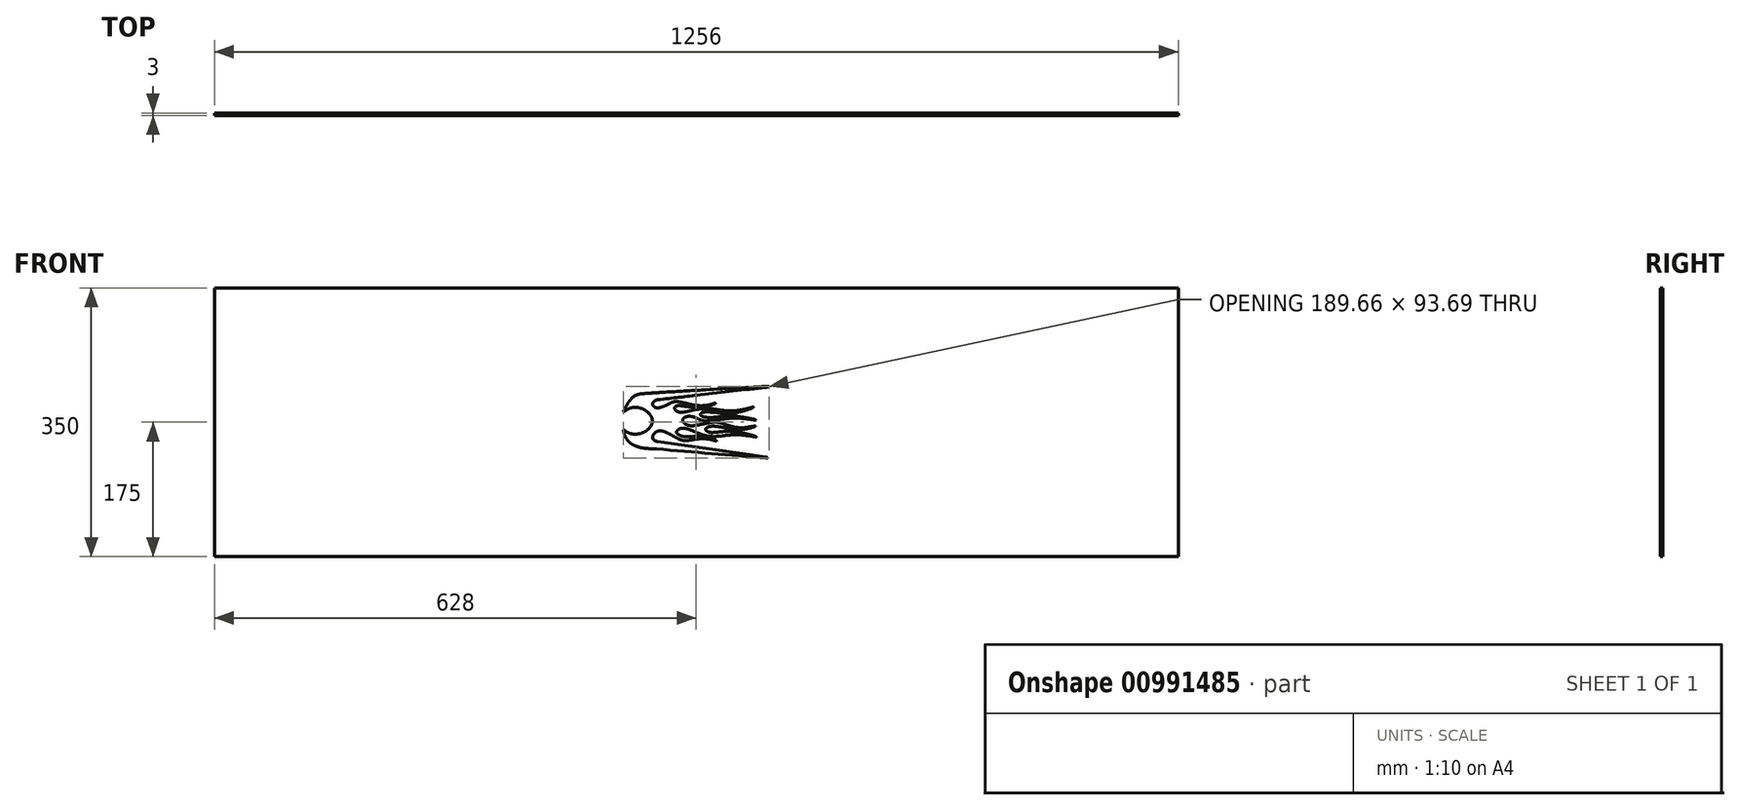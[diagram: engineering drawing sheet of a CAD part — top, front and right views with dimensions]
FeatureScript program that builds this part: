
annotation { "Feature Type Name" : "Feature", "Feature Type Description" : "" }
export const myFeature = defineFeature(function(context is Context, id is Id, definition is map)
    precondition{}
    {
        {
            var Q0;
            Q0=qCreatedBy(makeId("Front.planeOp"),FACE);
            var sketch = newSketch(context, id + "F0", { "sketchPlane" : qUnion([Q0])});
            skLineSegment(sketch, "E0.bottom", {"start": v(628, -175) * mm, "end": v(-628, -175) * mm});
            skLineSegment(sketch, "E0.top", {"start": v(628, 175) * mm, "end": v(-628, 175) * mm});
            skLineSegment(sketch, "E0.left", {"start": v(628, -175) * mm, "end": v(628, 175) * mm});
            skLineSegment(sketch, "E0.right", {"start": v(-628, -175) * mm, "end": v(-628, 175) * mm});
            skPoint(sketch, "E0.middle", {"position": v(0, 0) * mm});
            skArc(sketch, "E1", {"start": v(-49.97, 29.36) * mm, "mid": v(-22.29, 32.51) * mm, "end": v(5.39, 35.72) * mm});
            skArc(sketch, "E2", {"start": v(5.39, 35.72) * mm, "mid": v(48.23, 40.7) * mm, "end": v(91.08, 45.54) * mm});
            skArc(sketch, "E3", {"start": v(91.08, 45.54) * mm, "mid": v(92.6, 45.75) * mm, "end": v(94.1, 46.07) * mm});
            skArc(sketch, "E4", {"start": v(94.1, 46.07) * mm, "mid": v(94.42, 46.17) * mm, "end": v(94.72, 46.32) * mm});
            skArc(sketch, "E5", {"start": v(94.72, 46.32) * mm, "mid": v(94.82, 46.41) * mm, "end": v(94.81, 46.54) * mm});
            skArc(sketch, "E6", {"start": v(94.81, 46.54) * mm, "mid": v(94.26, 46.77) * mm, "end": v(93.66, 46.82) * mm});
            skArc(sketch, "E7", {"start": v(93.66, 46.82) * mm, "mid": v(92.36, 46.84) * mm, "end": v(91.07, 46.76) * mm});
            skArc(sketch, "E8", {"start": v(91.07, 46.76) * mm, "mid": v(90.64, 46.73) * mm, "end": v(90.2, 46.7) * mm});
            skArc(sketch, "E9", {"start": v(90.2, 46.7) * mm, "mid": v(48.75, 44.38) * mm, "end": v(7.3, 42.02) * mm});
            skArc(sketch, "E10", {"start": v(7.3, 42.02) * mm, "mid": v(-18.63, 40.5) * mm, "end": v(-44.56, 38.95) * mm});
            skArc(sketch, "E11", {"start": v(-44.56, 38.95) * mm, "mid": v(-53.35, 38.4) * mm, "end": v(-62.13, 37.81) * mm});
            skArc(sketch, "E12", {"start": v(-62.13, 37.81) * mm, "mid": v(-66.04, 37.54) * mm, "end": v(-69.95, 37.17) * mm});
            skArc(sketch, "E13", {"start": v(-69.95, 37.17) * mm, "mid": v(-78.19, 35.35) * mm, "end": v(-85.02, 30.4) * mm});
            skArc(sketch, "E14", {"start": v(-85.02, 30.4) * mm, "mid": v(-87.57, 27.3) * mm, "end": v(-89.78, 23.94) * mm});
            skArc(sketch, "E15", {"start": v(-89.78, 23.94) * mm, "mid": v(-91.8, 20.36) * mm, "end": v(-93.7, 16.7) * mm});
            skArc(sketch, "E16", {"start": v(-93.7, 16.7) * mm, "mid": v(-93.9, 16.3) * mm, "end": v(-94.1, 15.91) * mm});
            skArc(sketch, "E17", {"start": v(-94.1, 15.91) * mm, "mid": v(-94.48, 15.13) * mm, "end": v(-94.71, 14.3) * mm});
            skArc(sketch, "E18", {"start": v(-94.71, 14.3) * mm, "mid": v(-94.68, 14) * mm, "end": v(-94.42, 13.85) * mm});
            skArc(sketch, "E19", {"start": v(-94.42, 13.85) * mm, "mid": v(-93.65, 14.08) * mm, "end": v(-92.96, 14.48) * mm});
            skArc(sketch, "E20", {"start": v(-92.96, 14.48) * mm, "mid": v(-92.85, 14.55) * mm, "end": v(-92.73, 14.61) * mm});
            skArc(sketch, "E21", {"start": v(-92.73, 14.61) * mm, "mid": v(-87.36, 17.9) * mm, "end": v(-81.24, 19.36) * mm});
            skArc(sketch, "E22", {"start": v(-81.24, 19.36) * mm, "mid": v(-75.37, 19.02) * mm, "end": v(-69.75, 17.24) * mm});
            skArc(sketch, "E23", {"start": v(-69.75, 17.24) * mm, "mid": v(-64.93, 14.44) * mm, "end": v(-60.85, 10.63) * mm});
            skArc(sketch, "E24", {"start": v(-60.85, 10.63) * mm, "mid": v(-59.37, 8.6) * mm, "end": v(-58.18, 6.38) * mm});
            skArc(sketch, "E25", {"start": v(-58.18, 6.38) * mm, "mid": v(-57.44, 4.2) * mm, "end": v(-57.13, 1.9) * mm});
            skArc(sketch, "E26", {"start": v(-57.13, 1.9) * mm, "mid": v(-57.38, -0.44) * mm, "end": v(-58.06, -2.7) * mm});
            skArc(sketch, "E27", {"start": v(-58.06, -2.7) * mm, "mid": v(-59.2, -4.92) * mm, "end": v(-60.65, -6.95) * mm});
            skArc(sketch, "E28", {"start": v(-60.65, -6.95) * mm, "mid": v(-64.68, -10.72) * mm, "end": v(-69.48, -13.45) * mm});
            skArc(sketch, "E29", {"start": v(-69.48, -13.45) * mm, "mid": v(-75.15, -15.17) * mm, "end": v(-81.07, -15.5) * mm});
            skArc(sketch, "E30", {"start": v(-81.07, -15.5) * mm, "mid": v(-87.28, -14.14) * mm, "end": v(-92.84, -11.04) * mm});
            skArc(sketch, "E31", {"start": v(-92.84, -11.04) * mm, "mid": v(-93.32, -10.6) * mm, "end": v(-93.83, -10.2) * mm});
            skArc(sketch, "E32", {"start": v(-93.83, -10.2) * mm, "mid": v(-94.15, -10) * mm, "end": v(-94.53, -9.95) * mm});
            skArc(sketch, "E33", {"start": v(-94.53, -9.95) * mm, "mid": v(-94.78, -10.21) * mm, "end": v(-94.82, -10.58) * mm});
            skArc(sketch, "E34", {"start": v(-94.82, -10.58) * mm, "mid": v(-94.77, -11.47) * mm, "end": v(-94.6, -12.36) * mm});
            skArc(sketch, "E35", {"start": v(-94.6, -12.36) * mm, "mid": v(-93.25, -17.04) * mm, "end": v(-91.06, -21.4) * mm});
            skArc(sketch, "E36", {"start": v(-91.06, -21.4) * mm, "mid": v(-88.7, -24.49) * mm, "end": v(-85.85, -27.13) * mm});
            skArc(sketch, "E37", {"start": v(-85.85, -27.13) * mm, "mid": v(-83.19, -28.92) * mm, "end": v(-80.33, -30.38) * mm});
            skArc(sketch, "E38", {"start": v(-80.33, -30.38) * mm, "mid": v(-78.13, -31.26) * mm, "end": v(-75.88, -32.02) * mm});
            skArc(sketch, "E39", {"start": v(-75.88, -32.02) * mm, "mid": v(-75.4, -32.17) * mm, "end": v(-74.93, -32.33) * mm});
            skArc(sketch, "E40", {"start": v(-74.93, -32.33) * mm, "mid": v(-72.38, -33.1) * mm, "end": v(-69.75, -33.57) * mm});
            skArc(sketch, "E41", {"start": v(-69.75, -33.57) * mm, "mid": v(-66.23, -34) * mm, "end": v(-62.7, -34.32) * mm});
            skArc(sketch, "E42", {"start": v(-62.7, -34.32) * mm, "mid": v(-57.3, -34.63) * mm, "end": v(-51.9, -34.72) * mm});
            skArc(sketch, "E43", {"start": v(-51.9, -34.72) * mm, "mid": v(19.58, -40.8) * mm, "end": v(91.07, -46.8) * mm});
            skArc(sketch, "E44", {"start": v(91.07, -46.8) * mm, "mid": v(91.84, -46.84) * mm, "end": v(92.6, -46.75) * mm});
            skArc(sketch, "E45", {"start": v(92.6, -46.75) * mm, "mid": v(92.87, -46.66) * mm, "end": v(92.98, -46.4) * mm});
            skArc(sketch, "E46", {"start": v(92.98, -46.4) * mm, "mid": v(92.75, -46.12) * mm, "end": v(92.44, -45.94) * mm});
            skArc(sketch, "E47", {"start": v(92.44, -45.94) * mm, "mid": v(91.83, -45.73) * mm, "end": v(91.2, -45.6) * mm});
            skArc(sketch, "E48", {"start": v(91.2, -45.6) * mm, "mid": v(56.21, -40.64) * mm, "end": v(21.24, -35.54) * mm});
            skArc(sketch, "E49", {"start": v(21.24, -35.54) * mm, "mid": v(-14.89, -30.26) * mm, "end": v(-51.01, -24.96) * mm});
            skArc(sketch, "E50", {"start": v(-51.01, -24.96) * mm, "mid": v(-52.44, -24.6) * mm, "end": v(-53.8, -24.06) * mm});
            skArc(sketch, "E51", {"start": v(-53.8, -24.06) * mm, "mid": v(-54.77, -23.47) * mm, "end": v(-55.6, -22.71) * mm});
            skArc(sketch, "E52", {"start": v(-55.6, -22.71) * mm, "mid": v(-56.54, -21.08) * mm, "end": v(-56.76, -19.21) * mm});
            skArc(sketch, "E53", {"start": v(-56.76, -19.21) * mm, "mid": v(-55.5, -15.57) * mm, "end": v(-52.8, -12.83) * mm});
            skArc(sketch, "E54", {"start": v(-52.8, -12.83) * mm, "mid": v(-48.6, -11.31) * mm, "end": v(-44.12, -11.5) * mm});
            skArc(sketch, "E55", {"start": v(-44.12, -11.5) * mm, "mid": v(-42.1, -12.07) * mm, "end": v(-40.12, -12.82) * mm});
            skArc(sketch, "E56", {"start": v(-40.12, -12.82) * mm, "mid": v(-38.31, -13.65) * mm, "end": v(-36.53, -14.54) * mm});
            skArc(sketch, "E57", {"start": v(-36.53, -14.54) * mm, "mid": v(-35, -15.31) * mm, "end": v(-33.43, -16) * mm});
            skArc(sketch, "E58", {"start": v(-33.43, -16) * mm, "mid": v(-28.86, -18.7) * mm, "end": v(-24.18, -21.22) * mm});
            skArc(sketch, "E59", {"start": v(-24.18, -21.22) * mm, "mid": v(-21.02, -22.62) * mm, "end": v(-17.7, -23.6) * mm});
            skArc(sketch, "E60", {"start": v(-17.7, -23.6) * mm, "mid": v(-14.67, -23.93) * mm, "end": v(-11.63, -23.82) * mm});
            skArc(sketch, "E61", {"start": v(-11.63, -23.82) * mm, "mid": v(-7.64, -23.29) * mm, "end": v(-3.66, -22.6) * mm});
            skArc(sketch, "E62", {"start": v(-3.66, -22.6) * mm, "mid": v(-3.63, -22.6) * mm, "end": v(-3.6, -22.6) * mm});
            skArc(sketch, "E63", {"start": v(-3.6, -22.6) * mm, "mid": v(4.1, -21.59) * mm, "end": v(11.85, -21.58) * mm});
            skArc(sketch, "E64", {"start": v(11.85, -21.58) * mm, "mid": v(15.03, -21.86) * mm, "end": v(18.18, -22.35) * mm});
            skArc(sketch, "E65", {"start": v(18.18, -22.35) * mm, "mid": v(20.5, -22.87) * mm, "end": v(22.78, -23.6) * mm});
            skArc(sketch, "E66", {"start": v(22.78, -23.6) * mm, "mid": v(24.05, -24.01) * mm, "end": v(25.34, -24.3) * mm});
            skArc(sketch, "E67", {"start": v(25.34, -24.3) * mm, "mid": v(25.7, -24.33) * mm, "end": v(26.05, -24.32) * mm});
            skArc(sketch, "E68", {"start": v(26.05, -24.32) * mm, "mid": v(26.23, -24.29) * mm, "end": v(26.36, -24.18) * mm});
            skArc(sketch, "E69", {"start": v(26.36, -24.18) * mm, "mid": v(26.35, -24.02) * mm, "end": v(26.25, -23.9) * mm});
            skArc(sketch, "E70", {"start": v(26.25, -23.9) * mm, "mid": v(26, -23.68) * mm, "end": v(25.7, -23.5) * mm});
            skArc(sketch, "E71", {"start": v(25.7, -23.5) * mm, "mid": v(24.5, -22.95) * mm, "end": v(23.25, -22.53) * mm});
            skArc(sketch, "E72", {"start": v(23.25, -22.53) * mm, "mid": v(18.62, -21) * mm, "end": v(13.86, -19.88) * mm});
            skArc(sketch, "E73", {"start": v(13.86, -19.88) * mm, "mid": v(6.65, -18.77) * mm, "end": v(-0.64, -18.4) * mm});
            skArc(sketch, "E74", {"start": v(-0.64, -18.4) * mm, "mid": v(-2.99, -18.5) * mm, "end": v(-5.33, -18.62) * mm});
            skArc(sketch, "E75", {"start": v(-5.33, -18.62) * mm, "mid": v(-10.14, -18.85) * mm, "end": v(-14.96, -18.7) * mm});
            skArc(sketch, "E76", {"start": v(-14.96, -18.7) * mm, "mid": v(-19.53, -17.83) * mm, "end": v(-23.77, -15.9) * mm});
            skArc(sketch, "E77", {"start": v(-23.77, -15.9) * mm, "mid": v(-24.71, -15.01) * mm, "end": v(-25.37, -13.9) * mm});
            skArc(sketch, "E78", {"start": v(-25.37, -13.9) * mm, "mid": v(-25.55, -12.9) * mm, "end": v(-25.37, -11.9) * mm});
            skArc(sketch, "E79", {"start": v(-25.37, -11.9) * mm, "mid": v(-24.82, -10.88) * mm, "end": v(-24.04, -10.04) * mm});
            skArc(sketch, "E80", {"start": v(-24.04, -10.04) * mm, "mid": v(-22.88, -9.19) * mm, "end": v(-21.62, -8.51) * mm});
            skArc(sketch, "E81", {"start": v(-21.62, -8.51) * mm, "mid": v(-19.78, -7.95) * mm, "end": v(-17.87, -7.73) * mm});
            skArc(sketch, "E82", {"start": v(-17.87, -7.73) * mm, "mid": v(-15.9, -7.8) * mm, "end": v(-13.94, -8.1) * mm});
            skArc(sketch, "E83", {"start": v(-13.94, -8.1) * mm, "mid": v(-9.95, -9.23) * mm, "end": v(-6.06, -10.68) * mm});
            skArc(sketch, "E84", {"start": v(-6.06, -10.68) * mm, "mid": v(-4.72, -11.2) * mm, "end": v(-3.38, -11.7) * mm});
            skArc(sketch, "E85", {"start": v(-3.38, -11.7) * mm, "mid": v(-3.08, -11.82) * mm, "end": v(-2.79, -11.95) * mm});
            skArc(sketch, "E86", {"start": v(-2.79, -11.95) * mm, "mid": v(2.14, -14.05) * mm, "end": v(7.15, -15.93) * mm});
            skArc(sketch, "E87", {"start": v(7.15, -15.93) * mm, "mid": v(12.53, -17.47) * mm, "end": v(18.06, -18.31) * mm});
            skArc(sketch, "E88", {"start": v(18.06, -18.31) * mm, "mid": v(22.97, -18.5) * mm, "end": v(27.89, -18.35) * mm});
            skArc(sketch, "E89", {"start": v(27.89, -18.35) * mm, "mid": v(32.17, -17.96) * mm, "end": v(36.43, -17.45) * mm});
            skArc(sketch, "E90", {"start": v(36.43, -17.45) * mm, "mid": v(44.4, -16.58) * mm, "end": v(52.42, -16.3) * mm});
            skArc(sketch, "E91", {"start": v(52.42, -16.3) * mm, "mid": v(57.84, -16.5) * mm, "end": v(63.24, -16.99) * mm});
            skArc(sketch, "E92", {"start": v(63.24, -16.99) * mm, "mid": v(70.26, -17.96) * mm, "end": v(77.23, -19.23) * mm});
            skArc(sketch, "E93", {"start": v(77.23, -19.23) * mm, "mid": v(77.64, -19.3) * mm, "end": v(78.07, -19.33) * mm});
            skArc(sketch, "E94", {"start": v(78.07, -19.33) * mm, "mid": v(78.26, -19.3) * mm, "end": v(78.42, -19.19) * mm});
            skArc(sketch, "E95", {"start": v(78.42, -19.19) * mm, "mid": v(78.37, -19) * mm, "end": v(78.24, -18.88) * mm});
            skArc(sketch, "E96", {"start": v(78.24, -18.88) * mm, "mid": v(77.88, -18.65) * mm, "end": v(77.5, -18.47) * mm});
            skArc(sketch, "E97", {"start": v(77.5, -18.47) * mm, "mid": v(75.04, -17.64) * mm, "end": v(72.54, -16.93) * mm});
            skArc(sketch, "E98", {"start": v(72.54, -16.93) * mm, "mid": v(68.67, -15.94) * mm, "end": v(64.79, -15.02) * mm});
            skArc(sketch, "E99", {"start": v(64.79, -15.02) * mm, "mid": v(56.1, -13.24) * mm, "end": v(47.34, -11.91) * mm});
            skArc(sketch, "E100", {"start": v(47.34, -11.91) * mm, "mid": v(42.94, -11.7) * mm, "end": v(38.54, -11.84) * mm});
            skArc(sketch, "E101", {"start": v(38.54, -11.84) * mm, "mid": v(33.87, -12.22) * mm, "end": v(29.22, -12.7) * mm});
            skArc(sketch, "E102", {"start": v(29.22, -12.7) * mm, "mid": v(25.97, -13.05) * mm, "end": v(22.71, -13.33) * mm});
            skArc(sketch, "E103", {"start": v(22.71, -13.33) * mm, "mid": v(20.48, -13.43) * mm, "end": v(18.25, -13.28) * mm});
            skArc(sketch, "E104", {"start": v(18.25, -13.28) * mm, "mid": v(16.63, -12.85) * mm, "end": v(15.05, -12.28) * mm});
            skArc(sketch, "E105", {"start": v(15.05, -12.28) * mm, "mid": v(14.02, -11.8) * mm, "end": v(13.07, -11.17) * mm});
            skArc(sketch, "E106", {"start": v(13.07, -11.17) * mm, "mid": v(12.54, -10.64) * mm, "end": v(12.17, -9.99) * mm});
            skArc(sketch, "E107", {"start": v(12.17, -9.99) * mm, "mid": v(12.07, -9.4) * mm, "end": v(12.18, -8.82) * mm});
            skArc(sketch, "E108", {"start": v(12.18, -8.82) * mm, "mid": v(13.08, -7.58) * mm, "end": v(14.35, -6.71) * mm});
            skArc(sketch, "E109", {"start": v(14.35, -6.71) * mm, "mid": v(16.3, -5.87) * mm, "end": v(18.35, -5.34) * mm});
            skArc(sketch, "E110", {"start": v(18.35, -5.34) * mm, "mid": v(20.83, -5.1) * mm, "end": v(23.32, -5.1) * mm});
            skArc(sketch, "E111", {"start": v(23.32, -5.1) * mm, "mid": v(26.2, -5.31) * mm, "end": v(29.05, -5.67) * mm});
            skArc(sketch, "E112", {"start": v(29.05, -5.67) * mm, "mid": v(35.07, -6.7) * mm, "end": v(41.04, -7.93) * mm});
            skArc(sketch, "E113", {"start": v(41.04, -7.93) * mm, "mid": v(46.1, -8.99) * mm, "end": v(51.19, -9.77) * mm});
            skArc(sketch, "E114", {"start": v(51.19, -9.77) * mm, "mid": v(57.58, -9.66) * mm, "end": v(63.92, -8.85) * mm});
            skArc(sketch, "E115", {"start": v(63.92, -8.85) * mm, "mid": v(70.13, -7.48) * mm, "end": v(76.2, -5.61) * mm});
            skArc(sketch, "E116", {"start": v(76.2, -5.61) * mm, "mid": v(76.57, -5.47) * mm, "end": v(76.9, -5.28) * mm});
            skArc(sketch, "E117", {"start": v(76.9, -5.28) * mm, "mid": v(77.04, -5.17) * mm, "end": v(77.1, -5) * mm});
            skArc(sketch, "E118", {"start": v(77.1, -5) * mm, "mid": v(76.99, -4.89) * mm, "end": v(76.83, -4.86) * mm});
            skArc(sketch, "E119", {"start": v(76.83, -4.86) * mm, "mid": v(76.46, -4.86) * mm, "end": v(76.1, -4.91) * mm});
            skArc(sketch, "E120", {"start": v(76.1, -4.91) * mm, "mid": v(76.04, -4.92) * mm, "end": v(75.98, -4.93) * mm});
            skArc(sketch, "E121", {"start": v(75.98, -4.93) * mm, "mid": v(71.08, -5.82) * mm, "end": v(66.15, -6.59) * mm});
            skArc(sketch, "E122", {"start": v(66.15, -6.59) * mm, "mid": v(58.72, -7.25) * mm, "end": v(51.3, -6.57) * mm});
            skArc(sketch, "E123", {"start": v(51.3, -6.57) * mm, "mid": v(44.85, -5.06) * mm, "end": v(38.52, -3.08) * mm});
            skArc(sketch, "E124", {"start": v(38.52, -3.08) * mm, "mid": v(34.64, -1.84) * mm, "end": v(30.72, -0.74) * mm});
            skArc(sketch, "E125", {"start": v(30.72, -0.74) * mm, "mid": v(27.03, -0.03) * mm, "end": v(23.27, 0.22) * mm});
            skArc(sketch, "E126", {"start": v(23.27, 0.22) * mm, "mid": v(20.42, -0.06) * mm, "end": v(17.6, -0.53) * mm});
            skArc(sketch, "E127", {"start": v(17.6, -0.53) * mm, "mid": v(13.73, -1.28) * mm, "end": v(9.87, -2.07) * mm});
            skArc(sketch, "E128", {"start": v(9.87, -2.07) * mm, "mid": v(5.06, -3.06) * mm, "end": v(0.23, -3.96) * mm});
            skArc(sketch, "E129", {"start": v(0.23, -3.96) * mm, "mid": v(-1.8, -4.28) * mm, "end": v(-3.83, -4.54) * mm});
            skArc(sketch, "E130", {"start": v(-3.83, -4.54) * mm, "mid": v(-5.35, -4.67) * mm, "end": v(-6.88, -4.67) * mm});
            skArc(sketch, "E131", {"start": v(-6.88, -4.67) * mm, "mid": v(-10.85, -3.87) * mm, "end": v(-14.52, -2.16) * mm});
            skArc(sketch, "E132", {"start": v(-14.52, -2.16) * mm, "mid": v(-15.65, -1.27) * mm, "end": v(-16.62, -0.2) * mm});
            skArc(sketch, "E133", {"start": v(-16.62, -0.2) * mm, "mid": v(-17.22, 0.82) * mm, "end": v(-17.56, 1.94) * mm});
            skArc(sketch, "E134", {"start": v(-17.56, 1.94) * mm, "mid": v(-17.3, 4.12) * mm, "end": v(-15.91, 5.83) * mm});
            skArc(sketch, "E135", {"start": v(-15.91, 5.83) * mm, "mid": v(-14.66, 6.6) * mm, "end": v(-13.29, 7.12) * mm});
            skArc(sketch, "E136", {"start": v(-13.29, 7.12) * mm, "mid": v(-11.38, 7.53) * mm, "end": v(-9.44, 7.68) * mm});
            skArc(sketch, "E137", {"start": v(-9.44, 7.68) * mm, "mid": v(-6.11, 7.46) * mm, "end": v(-2.85, 6.72) * mm});
            skArc(sketch, "E138", {"start": v(-2.85, 6.72) * mm, "mid": v(-0.4, 5.77) * mm, "end": v(1.95, 4.6) * mm});
            skArc(sketch, "E139", {"start": v(1.95, 4.6) * mm, "mid": v(5.08, 3.1) * mm, "end": v(8.39, 2.02) * mm});
            skArc(sketch, "E140", {"start": v(8.39, 2.02) * mm, "mid": v(10.6, 1.61) * mm, "end": v(12.83, 1.43) * mm});
            skArc(sketch, "E141", {"start": v(12.83, 1.43) * mm, "mid": v(15.8, 1.45) * mm, "end": v(18.74, 1.7) * mm});
            skArc(sketch, "E142", {"start": v(18.74, 1.7) * mm, "mid": v(21.42, 2.12) * mm, "end": v(24.1, 2.56) * mm});
            skArc(sketch, "E143", {"start": v(24.1, 2.56) * mm, "mid": v(32.98, 3.95) * mm, "end": v(41.9, 5.02) * mm});
            skArc(sketch, "E144", {"start": v(41.9, 5.02) * mm, "mid": v(51.02, 5.47) * mm, "end": v(60.14, 4.97) * mm});
            skArc(sketch, "E145", {"start": v(60.14, 4.97) * mm, "mid": v(68.02, 4.05) * mm, "end": v(75.88, 2.92) * mm});
            skArc(sketch, "E146", {"start": v(75.88, 2.92) * mm, "mid": v(76.5, 2.83) * mm, "end": v(77.14, 2.8) * mm});
            skArc(sketch, "E147", {"start": v(77.14, 2.8) * mm, "mid": v(77.35, 2.82) * mm, "end": v(77.5, 2.98) * mm});
            skArc(sketch, "E148", {"start": v(77.5, 2.98) * mm, "mid": v(77.35, 3.17) * mm, "end": v(77.13, 3.29) * mm});
            skArc(sketch, "E149", {"start": v(77.13, 3.29) * mm, "mid": v(76.65, 3.47) * mm, "end": v(76.16, 3.58) * mm});
            skArc(sketch, "E150", {"start": v(76.16, 3.58) * mm, "mid": v(75.47, 3.72) * mm, "end": v(74.79, 3.86) * mm});
            skArc(sketch, "E151", {"start": v(74.79, 3.86) * mm, "mid": v(67.42, 5.33) * mm, "end": v(60.02, 6.65) * mm});
            skArc(sketch, "E152", {"start": v(60.02, 6.65) * mm, "mid": v(55.46, 7.36) * mm, "end": v(50.89, 7.95) * mm});
            skArc(sketch, "E153", {"start": v(50.89, 7.95) * mm, "mid": v(47.14, 8.3) * mm, "end": v(43.37, 8.38) * mm});
            skArc(sketch, "E154", {"start": v(43.37, 8.38) * mm, "mid": v(40.5, 8.3) * mm, "end": v(37.62, 8.07) * mm});
            skArc(sketch, "E155", {"start": v(37.62, 8.07) * mm, "mid": v(34.46, 7.71) * mm, "end": v(31.3, 7.31) * mm});
            skArc(sketch, "E156", {"start": v(31.3, 7.31) * mm, "mid": v(26.2, 6.68) * mm, "end": v(21.07, 6.23) * mm});
            skArc(sketch, "E157", {"start": v(21.07, 6.23) * mm, "mid": v(16.22, 6.14) * mm, "end": v(11.4, 6.64) * mm});
            skArc(sketch, "E158", {"start": v(11.4, 6.64) * mm, "mid": v(9, 7.24) * mm, "end": v(6.76, 8.29) * mm});
            skArc(sketch, "E159", {"start": v(6.76, 8.29) * mm, "mid": v(6.16, 8.75) * mm, "end": v(5.66, 9.33) * mm});
            skArc(sketch, "E160", {"start": v(5.66, 9.33) * mm, "mid": v(5.41, 9.85) * mm, "end": v(5.35, 10.42) * mm});
            skArc(sketch, "E161", {"start": v(5.35, 10.42) * mm, "mid": v(5.5, 10.97) * mm, "end": v(5.82, 11.45) * mm});
            skArc(sketch, "E162", {"start": v(5.82, 11.45) * mm, "mid": v(6.4, 11.96) * mm, "end": v(7.05, 12.35) * mm});
            skArc(sketch, "E163", {"start": v(7.05, 12.35) * mm, "mid": v(9.35, 13.11) * mm, "end": v(11.75, 13.41) * mm});
            skArc(sketch, "E164", {"start": v(11.75, 13.41) * mm, "mid": v(15.6, 13.4) * mm, "end": v(19.44, 13.2) * mm});
            skArc(sketch, "E165", {"start": v(19.44, 13.2) * mm, "mid": v(23.59, 12.92) * mm, "end": v(27.72, 12.47) * mm});
            skArc(sketch, "E166", {"start": v(27.72, 12.47) * mm, "mid": v(39.73, 11.7) * mm, "end": v(51.73, 12.63) * mm});
            skArc(sketch, "E167", {"start": v(51.73, 12.63) * mm, "mid": v(62.5, 15.04) * mm, "end": v(72.9, 18.74) * mm});
            skArc(sketch, "E168", {"start": v(72.9, 18.74) * mm, "mid": v(73.48, 18.94) * mm, "end": v(74.05, 19.2) * mm});
            skArc(sketch, "E169", {"start": v(74.05, 19.2) * mm, "mid": v(74.3, 19.35) * mm, "end": v(74.46, 19.58) * mm});
            skArc(sketch, "E170", {"start": v(74.46, 19.58) * mm, "mid": v(74.31, 19.74) * mm, "end": v(74.1, 19.75) * mm});
            skArc(sketch, "E171", {"start": v(74.1, 19.75) * mm, "mid": v(73.49, 19.7) * mm, "end": v(72.9, 19.57) * mm});
            skArc(sketch, "E172", {"start": v(72.9, 19.57) * mm, "mid": v(63.37, 17.07) * mm, "end": v(53.68, 15.27) * mm});
            skArc(sketch, "E173", {"start": v(53.68, 15.27) * mm, "mid": v(44.03, 14.6) * mm, "end": v(34.4, 15.4) * mm});
            skArc(sketch, "E174", {"start": v(34.4, 15.4) * mm, "mid": v(33.15, 15.59) * mm, "end": v(31.9, 15.77) * mm});
            skArc(sketch, "E175", {"start": v(31.9, 15.77) * mm, "mid": v(26.34, 16.6) * mm, "end": v(20.77, 17.31) * mm});
            skArc(sketch, "E176", {"start": v(20.77, 17.31) * mm, "mid": v(16.06, 17.7) * mm, "end": v(11.33, 17.8) * mm});
            skArc(sketch, "E177", {"start": v(11.33, 17.8) * mm, "mid": v(6.17, 17.48) * mm, "end": v(1.05, 16.8) * mm});
            skArc(sketch, "E178", {"start": v(1.05, 16.8) * mm, "mid": v(-5.82, 15.47) * mm, "end": v(-12.64, 13.89) * mm});
            skArc(sketch, "E179", {"start": v(-12.64, 13.89) * mm, "mid": v(-12.98, 13.82) * mm, "end": v(-13.33, 13.75) * mm});
            skArc(sketch, "E180", {"start": v(-13.33, 13.75) * mm, "mid": v(-16.32, 13.2) * mm, "end": v(-19.35, 12.93) * mm});
            skArc(sketch, "E181", {"start": v(-19.35, 12.93) * mm, "mid": v(-22.45, 13.21) * mm, "end": v(-25.37, 14.27) * mm});
            skArc(sketch, "E182", {"start": v(-25.37, 14.27) * mm, "mid": v(-27.32, 15.87) * mm, "end": v(-28.22, 18.24) * mm});
            skArc(sketch, "E183", {"start": v(-28.22, 18.24) * mm, "mid": v(-27.94, 19.5) * mm, "end": v(-27.1, 20.5) * mm});
            skArc(sketch, "E184", {"start": v(-27.1, 20.5) * mm, "mid": v(-26.33, 20.98) * mm, "end": v(-25.49, 21.32) * mm});
            skArc(sketch, "E185", {"start": v(-25.49, 21.32) * mm, "mid": v(-24.26, 21.62) * mm, "end": v(-23, 21.78) * mm});
            skArc(sketch, "E186", {"start": v(-23, 21.78) * mm, "mid": v(-21.84, 21.75) * mm, "end": v(-20.7, 21.62) * mm});
            skArc(sketch, "E187", {"start": v(-20.7, 21.62) * mm, "mid": v(-18.75, 21.37) * mm, "end": v(-16.8, 21.09) * mm});
            skArc(sketch, "E188", {"start": v(-16.8, 21.09) * mm, "mid": v(-9.62, 20.12) * mm, "end": v(-2.4, 19.46) * mm});
            skArc(sketch, "E189", {"start": v(-2.4, 19.46) * mm, "mid": v(1.54, 19.32) * mm, "end": v(5.48, 19.4) * mm});
            skArc(sketch, "E190", {"start": v(5.48, 19.4) * mm, "mid": v(9.07, 19.73) * mm, "end": v(12.6, 20.44) * mm});
            skArc(sketch, "E191", {"start": v(12.6, 20.44) * mm, "mid": v(15.62, 21.14) * mm, "end": v(18.6, 21.93) * mm});
            skArc(sketch, "E192", {"start": v(18.6, 21.93) * mm, "mid": v(21.41, 22.85) * mm, "end": v(24.14, 24) * mm});
            skArc(sketch, "E193", {"start": v(24.14, 24) * mm, "mid": v(24.52, 24.2) * mm, "end": v(24.86, 24.47) * mm});
            skArc(sketch, "E194", {"start": v(24.86, 24.47) * mm, "mid": v(25, 24.62) * mm, "end": v(25.04, 24.83) * mm});
            skArc(sketch, "E195", {"start": v(25.04, 24.83) * mm, "mid": v(24.9, 24.96) * mm, "end": v(24.7, 24.98) * mm});
            skArc(sketch, "E196", {"start": v(24.7, 24.98) * mm, "mid": v(24.27, 24.92) * mm, "end": v(23.85, 24.8) * mm});
            skArc(sketch, "E197", {"start": v(23.85, 24.8) * mm, "mid": v(20.09, 23.58) * mm, "end": v(16.26, 22.59) * mm});
            skArc(sketch, "E198", {"start": v(16.26, 22.59) * mm, "mid": v(12.22, 21.88) * mm, "end": v(8.14, 21.54) * mm});
            skArc(sketch, "E199", {"start": v(8.14, 21.54) * mm, "mid": v(3.4, 21.6) * mm, "end": v(-1.32, 22.09) * mm});
            skArc(sketch, "E200", {"start": v(-1.32, 22.09) * mm, "mid": v(-7.15, 23.19) * mm, "end": v(-12.9, 24.7) * mm});
            skArc(sketch, "E201", {"start": v(-12.9, 24.7) * mm, "mid": v(-15.34, 25.13) * mm, "end": v(-17.77, 25.67) * mm});
            skArc(sketch, "E202", {"start": v(-17.77, 25.67) * mm, "mid": v(-21.61, 26.48) * mm, "end": v(-25.5, 26.96) * mm});
            skArc(sketch, "E203", {"start": v(-25.5, 26.96) * mm, "mid": v(-29.3, 26.71) * mm, "end": v(-32.87, 25.39) * mm});
            skArc(sketch, "E204", {"start": v(-32.87, 25.39) * mm, "mid": v(-36.24, 23.61) * mm, "end": v(-39.68, 21.96) * mm});
            skArc(sketch, "E205", {"start": v(-39.68, 21.96) * mm, "mid": v(-43.16, 20.52) * mm, "end": v(-46.73, 19.32) * mm});
            skArc(sketch, "E206", {"start": v(-46.73, 19.32) * mm, "mid": v(-48.6, 18.9) * mm, "end": v(-50.5, 18.76) * mm});
            skArc(sketch, "E207", {"start": v(-50.5, 18.76) * mm, "mid": v(-52.01, 18.9) * mm, "end": v(-53.47, 19.3) * mm});
            skArc(sketch, "E208", {"start": v(-53.47, 19.3) * mm, "mid": v(-55.42, 20.54) * mm, "end": v(-56.63, 22.51) * mm});
            skArc(sketch, "E209", {"start": v(-56.63, 22.51) * mm, "mid": v(-56.67, 24.7) * mm, "end": v(-55.65, 26.64) * mm});
            skArc(sketch, "E210", {"start": v(-55.65, 26.64) * mm, "mid": v(-54.63, 27.6) * mm, "end": v(-53.44, 28.32) * mm});
            skArc(sketch, "E211", {"start": v(-53.44, 28.32) * mm, "mid": v(-51.75, 28.97) * mm, "end": v(-49.97, 29.36) * mm});
            skArc(sketch, "E212", {"start": v(-57.07, 25.24) * mm, "mid": v(-57.2, 22.6) * mm, "end": v(-55.93, 20.3) * mm});
            skArc(sketch, "E213", {"start": v(-55.93, 20.3) * mm, "mid": v(-54.12, 19) * mm, "end": v(-51.98, 18.36) * mm});
            skArc(sketch, "E214", {"start": v(-51.98, 18.36) * mm, "mid": v(-49.26, 18.3) * mm, "end": v(-46.58, 18.81) * mm});
            skArc(sketch, "E215", {"start": v(-46.58, 18.81) * mm, "mid": v(-42.84, 20.07) * mm, "end": v(-39.2, 21.6) * mm});
            skArc(sketch, "E216", {"start": v(-39.2, 21.6) * mm, "mid": v(-35.88, 23.2) * mm, "end": v(-32.61, 24.92) * mm});
            skArc(sketch, "E217", {"start": v(-32.61, 24.92) * mm, "mid": v(-29.16, 26.2) * mm, "end": v(-25.49, 26.43) * mm});
            skArc(sketch, "E218", {"start": v(-25.49, 26.43) * mm, "mid": v(-21.66, 25.95) * mm, "end": v(-17.9, 25.15) * mm});
            skArc(sketch, "E219", {"start": v(-17.9, 25.15) * mm, "mid": v(-15.46, 24.62) * mm, "end": v(-13, 24.18) * mm});
            skLineSegment(sketch, "E220", {"start": v(-13, 24.18) * mm, "end": v(-13.04, 24.19) * mm});
            skLineSegment(sketch, "E221", {"start": v(-13.04, 24.19) * mm, "end": v(-12.97, 24.17) * mm});
            skArc(sketch, "E222", {"start": v(-12.97, 24.17) * mm, "mid": v(-12.98, 24.17) * mm, "end": v(-13, 24.17) * mm});
            skArc(sketch, "E223", {"start": v(-13, 24.17) * mm, "mid": v(-13, 24.18) * mm, "end": v(-13, 24.18) * mm});
            skArc(sketch, "E224", {"start": v(-13, 24.18) * mm, "mid": v(-6.1, 22.4) * mm, "end": v(0.93, 21.27) * mm});
            skArc(sketch, "E225", {"start": v(0.93, 21.27) * mm, "mid": v(6.57, 20.98) * mm, "end": v(12.2, 21.35) * mm});
            skArc(sketch, "E226", {"start": v(12.2, 21.35) * mm, "mid": v(13.51, 21.53) * mm, "end": v(14.83, 21.6) * mm});
            skArc(sketch, "E227", {"start": v(14.83, 21.6) * mm, "mid": v(14.6, 21.46) * mm, "end": v(14.32, 21.4) * mm});
            skArc(sketch, "E228", {"start": v(14.32, 21.4) * mm, "mid": v(13.4, 21.17) * mm, "end": v(12.5, 20.96) * mm});
            skArc(sketch, "E229", {"start": v(12.5, 20.96) * mm, "mid": v(8.98, 20.25) * mm, "end": v(5.41, 19.92) * mm});
            skArc(sketch, "E230", {"start": v(5.41, 19.92) * mm, "mid": v(1.5, 19.85) * mm, "end": v(-2.42, 20) * mm});
            skArc(sketch, "E231", {"start": v(-2.42, 20) * mm, "mid": v(-9.59, 20.65) * mm, "end": v(-16.73, 21.61) * mm});
            skLineSegment(sketch, "E232", {"start": v(-16.73, 21.61) * mm, "end": v(-16.73, 21.61) * mm});
            skArc(sketch, "E233", {"start": v(-16.73, 21.61) * mm, "mid": v(-18.7, 21.9) * mm, "end": v(-20.68, 22.16) * mm});
            skArc(sketch, "E234", {"start": v(-20.68, 22.16) * mm, "mid": v(-21.86, 22.28) * mm, "end": v(-23.05, 22.3) * mm});
            skArc(sketch, "E235", {"start": v(-23.05, 22.3) * mm, "mid": v(-24.44, 22.12) * mm, "end": v(-25.8, 21.77) * mm});
            skArc(sketch, "E236", {"start": v(-25.8, 21.77) * mm, "mid": v(-26.68, 21.39) * mm, "end": v(-27.5, 20.86) * mm});
            skArc(sketch, "E237", {"start": v(-27.5, 20.86) * mm, "mid": v(-28.29, 19.96) * mm, "end": v(-28.7, 18.84) * mm});
            skArc(sketch, "E238", {"start": v(-28.7, 18.84) * mm, "mid": v(-28.6, 17.25) * mm, "end": v(-27.94, 15.81) * mm});
            skArc(sketch, "E239", {"start": v(-27.94, 15.81) * mm, "mid": v(-26.9, 14.63) * mm, "end": v(-25.58, 13.78) * mm});
            skLineSegment(sketch, "E240", {"start": v(-25.58, 13.78) * mm, "end": v(-25.61, 13.8) * mm});
            skArc(sketch, "E241", {"start": v(-25.61, 13.8) * mm, "mid": v(-22.58, 12.7) * mm, "end": v(-19.36, 12.4) * mm});
            skArc(sketch, "E242", {"start": v(-19.36, 12.4) * mm, "mid": v(-16.28, 12.68) * mm, "end": v(-13.23, 13.23) * mm});
            skLineSegment(sketch, "E243", {"start": v(-13.23, 13.23) * mm, "end": v(-13.23, 13.23) * mm});
            skLineSegment(sketch, "E244", {"start": v(-13.23, 13.23) * mm, "end": v(-12.54, 13.37) * mm});
            skArc(sketch, "E245", {"start": v(-12.54, 13.37) * mm, "mid": v(-5.75, 14.95) * mm, "end": v(1.1, 16.26) * mm});
            skArc(sketch, "E246", {"start": v(1.1, 16.26) * mm, "mid": v(6.2, 16.94) * mm, "end": v(11.34, 17.26) * mm});
            skArc(sketch, "E247", {"start": v(11.34, 17.26) * mm, "mid": v(16.04, 17.18) * mm, "end": v(20.73, 16.78) * mm});
            skArc(sketch, "E248", {"start": v(20.73, 16.78) * mm, "mid": v(26.29, 16.07) * mm, "end": v(31.83, 15.25) * mm});
            skLineSegment(sketch, "E249", {"start": v(31.83, 15.25) * mm, "end": v(31.83, 15.25) * mm});
            skLineSegment(sketch, "E250", {"start": v(31.83, 15.25) * mm, "end": v(34.32, 14.88) * mm});
            skArc(sketch, "E251", {"start": v(34.32, 14.88) * mm, "mid": v(41.86, 14.1) * mm, "end": v(49.45, 14.27) * mm});
            skArc(sketch, "E252", {"start": v(49.45, 14.27) * mm, "mid": v(57.33, 15.3) * mm, "end": v(65.1, 16.94) * mm});
            skArc(sketch, "E253", {"start": v(65.1, 16.94) * mm, "mid": v(65.9, 17.13) * mm, "end": v(66.72, 17.29) * mm});
            skArc(sketch, "E254", {"start": v(66.72, 17.29) * mm, "mid": v(67.02, 17.34) * mm, "end": v(67.32, 17.32) * mm});
            skArc(sketch, "E255", {"start": v(67.32, 17.32) * mm, "mid": v(67.13, 17.14) * mm, "end": v(66.89, 17.05) * mm});
            skArc(sketch, "E256", {"start": v(66.89, 17.05) * mm, "mid": v(66.14, 16.77) * mm, "end": v(65.38, 16.51) * mm});
            skArc(sketch, "E257", {"start": v(65.38, 16.51) * mm, "mid": v(46.79, 12.58) * mm, "end": v(27.78, 13) * mm});
            skArc(sketch, "E258", {"start": v(27.78, 13) * mm, "mid": v(23.64, 13.44) * mm, "end": v(19.48, 13.73) * mm});
            skArc(sketch, "E259", {"start": v(19.48, 13.73) * mm, "mid": v(15.6, 13.93) * mm, "end": v(11.72, 13.94) * mm});
            skArc(sketch, "E260", {"start": v(11.72, 13.94) * mm, "mid": v(9.18, 13.61) * mm, "end": v(6.76, 12.8) * mm});
            skArc(sketch, "E261", {"start": v(6.76, 12.8) * mm, "mid": v(6, 12.34) * mm, "end": v(5.36, 11.74) * mm});
            skArc(sketch, "E262", {"start": v(5.36, 11.74) * mm, "mid": v(4.98, 11.13) * mm, "end": v(4.82, 10.43) * mm});
            skArc(sketch, "E263", {"start": v(4.82, 10.43) * mm, "mid": v(4.9, 9.7) * mm, "end": v(5.2, 9.05) * mm});
            skArc(sketch, "E264", {"start": v(5.2, 9.05) * mm, "mid": v(5.76, 8.39) * mm, "end": v(6.45, 7.85) * mm});
            skArc(sketch, "E265", {"start": v(6.45, 7.85) * mm, "mid": v(8.8, 6.75) * mm, "end": v(11.3, 6.12) * mm});
            skArc(sketch, "E266", {"start": v(11.3, 6.12) * mm, "mid": v(16.16, 5.61) * mm, "end": v(21.04, 5.7) * mm});
            skArc(sketch, "E267", {"start": v(21.04, 5.7) * mm, "mid": v(26.21, 6.15) * mm, "end": v(31.37, 6.79) * mm});
            skLineSegment(sketch, "E268", {"start": v(31.37, 6.79) * mm, "end": v(31.37, 6.8) * mm});
            skArc(sketch, "E269", {"start": v(31.37, 6.8) * mm, "mid": v(34.52, 7.19) * mm, "end": v(37.67, 7.54) * mm});
            skArc(sketch, "E270", {"start": v(37.67, 7.54) * mm, "mid": v(40.52, 7.77) * mm, "end": v(43.37, 7.85) * mm});
            skArc(sketch, "E271", {"start": v(43.37, 7.85) * mm, "mid": v(46.75, 7.79) * mm, "end": v(50.12, 7.5) * mm});
            skArc(sketch, "E272", {"start": v(50.12, 7.5) * mm, "mid": v(55.1, 6.87) * mm, "end": v(60.07, 6.1) * mm});
            skArc(sketch, "E273", {"start": v(60.07, 6.1) * mm, "mid": v(61.7, 5.82) * mm, "end": v(63.32, 5.52) * mm});
            skArc(sketch, "E274", {"start": v(63.32, 5.52) * mm, "mid": v(63.88, 5.42) * mm, "end": v(64.43, 5.24) * mm});
            skArc(sketch, "E275", {"start": v(64.43, 5.24) * mm, "mid": v(63.9, 5.18) * mm, "end": v(63.39, 5.23) * mm});
            skArc(sketch, "E276", {"start": v(63.39, 5.23) * mm, "mid": v(61.79, 5.35) * mm, "end": v(60.19, 5.5) * mm});
            skArc(sketch, "E277", {"start": v(60.19, 5.5) * mm, "mid": v(51.03, 6) * mm, "end": v(41.86, 5.55) * mm});
            skArc(sketch, "E278", {"start": v(41.86, 5.55) * mm, "mid": v(32.92, 4.47) * mm, "end": v(24.02, 3.08) * mm});
            skLineSegment(sketch, "E279", {"start": v(24.02, 3.08) * mm, "end": v(18.66, 2.22) * mm});
            skArc(sketch, "E280", {"start": v(18.66, 2.22) * mm, "mid": v(15.77, 1.97) * mm, "end": v(12.87, 1.96) * mm});
            skArc(sketch, "E281", {"start": v(12.87, 1.96) * mm, "mid": v(10.67, 2.14) * mm, "end": v(8.5, 2.54) * mm});
            skArc(sketch, "E282", {"start": v(8.5, 2.54) * mm, "mid": v(5.26, 3.6) * mm, "end": v(2.19, 5.08) * mm});
            skLineSegment(sketch, "E283", {"start": v(2.19, 5.08) * mm, "end": v(2.19, 5.08) * mm});
            skArc(sketch, "E284", {"start": v(2.19, 5.08) * mm, "mid": v(-0.2, 6.25) * mm, "end": v(-2.68, 7.22) * mm});
            skArc(sketch, "E285", {"start": v(-2.68, 7.22) * mm, "mid": v(-6.02, 7.98) * mm, "end": v(-9.44, 8.2) * mm});
            skArc(sketch, "E286", {"start": v(-9.44, 8.2) * mm, "mid": v(-11.46, 8.05) * mm, "end": v(-13.43, 7.63) * mm});
            skArc(sketch, "E287", {"start": v(-13.43, 7.63) * mm, "mid": v(-14.82, 7.1) * mm, "end": v(-16.1, 6.34) * mm});
            skArc(sketch, "E288", {"start": v(-16.1, 6.34) * mm, "mid": v(-17.53, 4.8) * mm, "end": v(-18.14, 2.78) * mm});
            skArc(sketch, "E289", {"start": v(-18.14, 2.78) * mm, "mid": v(-18, 1.47) * mm, "end": v(-17.51, 0.25) * mm});
            skArc(sketch, "E290", {"start": v(-17.51, 0.25) * mm, "mid": v(-16.6, -1.05) * mm, "end": v(-15.42, -2.14) * mm});
            skArc(sketch, "E291", {"start": v(-15.42, -2.14) * mm, "mid": v(-13.73, -3.24) * mm, "end": v(-11.9, -4.06) * mm});
            skArc(sketch, "E292", {"start": v(-11.9, -4.06) * mm, "mid": v(-9.45, -4.78) * mm, "end": v(-6.93, -5.2) * mm});
            skArc(sketch, "E293", {"start": v(-6.93, -5.2) * mm, "mid": v(-3.32, -5.03) * mm, "end": v(0.25, -4.5) * mm});
            skArc(sketch, "E294", {"start": v(0.25, -4.5) * mm, "mid": v(5.12, -3.58) * mm, "end": v(9.98, -2.59) * mm});
            skLineSegment(sketch, "E295", {"start": v(9.98, -2.59) * mm, "end": v(9.98, -2.59) * mm});
            skArc(sketch, "E296", {"start": v(9.98, -2.59) * mm, "mid": v(13.83, -1.8) * mm, "end": v(17.68, -1.05) * mm});
            skArc(sketch, "E297", {"start": v(17.68, -1.05) * mm, "mid": v(20.47, -0.59) * mm, "end": v(23.29, -0.31) * mm});
            skArc(sketch, "E298", {"start": v(23.29, -0.31) * mm, "mid": v(27, -0.56) * mm, "end": v(30.64, -1.27) * mm});
            skArc(sketch, "E299", {"start": v(30.64, -1.27) * mm, "mid": v(34.52, -2.36) * mm, "end": v(38.36, -3.59) * mm});
            skLineSegment(sketch, "E300", {"start": v(38.36, -3.59) * mm, "end": v(38.36, -3.59) * mm});
            skArc(sketch, "E301", {"start": v(38.36, -3.59) * mm, "mid": v(44.72, -5.57) * mm, "end": v(51.2, -7.08) * mm});
            skArc(sketch, "E302", {"start": v(51.2, -7.08) * mm, "mid": v(58.72, -7.78) * mm, "end": v(66.25, -7.1) * mm});
            skArc(sketch, "E303", {"start": v(66.25, -7.1) * mm, "mid": v(67.96, -6.9) * mm, "end": v(69.68, -6.71) * mm});
            skArc(sketch, "E304", {"start": v(69.68, -6.71) * mm, "mid": v(70.28, -6.65) * mm, "end": v(70.88, -6.7) * mm});
            skArc(sketch, "E305", {"start": v(70.88, -6.7) * mm, "mid": v(70.35, -6.94) * mm, "end": v(69.77, -7.07) * mm});
            skArc(sketch, "E306", {"start": v(69.77, -7.07) * mm, "mid": v(68.03, -7.47) * mm, "end": v(66.28, -7.85) * mm});
            skArc(sketch, "E307", {"start": v(66.28, -7.85) * mm, "mid": v(59.8, -8.91) * mm, "end": v(53.25, -9.15) * mm});
            skArc(sketch, "E308", {"start": v(53.25, -9.15) * mm, "mid": v(47.16, -8.55) * mm, "end": v(41.15, -7.42) * mm});
            skArc(sketch, "E309", {"start": v(41.15, -7.42) * mm, "mid": v(35.1, -6.17) * mm, "end": v(29, -5.12) * mm});
            skArc(sketch, "E310", {"start": v(29, -5.12) * mm, "mid": v(26.15, -4.77) * mm, "end": v(23.27, -4.57) * mm});
            skArc(sketch, "E311", {"start": v(23.27, -4.57) * mm, "mid": v(20.76, -4.57) * mm, "end": v(18.27, -4.81) * mm});
            skArc(sketch, "E312", {"start": v(18.27, -4.81) * mm, "mid": v(15.92, -5.44) * mm, "end": v(13.72, -6.47) * mm});
            skArc(sketch, "E313", {"start": v(13.72, -6.47) * mm, "mid": v(12.88, -7.06) * mm, "end": v(12.16, -7.79) * mm});
            skArc(sketch, "E314", {"start": v(12.16, -7.79) * mm, "mid": v(11.72, -8.53) * mm, "end": v(11.54, -9.37) * mm});
            skArc(sketch, "E315", {"start": v(11.54, -9.37) * mm, "mid": v(11.63, -10.07) * mm, "end": v(11.93, -10.71) * mm});
            skArc(sketch, "E316", {"start": v(11.93, -10.71) * mm, "mid": v(12.48, -11.37) * mm, "end": v(13.16, -11.9) * mm});
            skArc(sketch, "E317", {"start": v(13.16, -11.9) * mm, "mid": v(15.56, -13.06) * mm, "end": v(18.12, -13.8) * mm});
            skArc(sketch, "E318", {"start": v(18.12, -13.8) * mm, "mid": v(20.41, -13.96) * mm, "end": v(22.7, -13.86) * mm});
            skArc(sketch, "E319", {"start": v(22.7, -13.86) * mm, "mid": v(26, -13.58) * mm, "end": v(29.27, -13.23) * mm});
            skLineSegment(sketch, "E320", {"start": v(29.27, -13.23) * mm, "end": v(29.27, -13.23) * mm});
            skArc(sketch, "E321", {"start": v(29.27, -13.23) * mm, "mid": v(33.93, -12.75) * mm, "end": v(38.59, -12.37) * mm});
            skArc(sketch, "E322", {"start": v(38.59, -12.37) * mm, "mid": v(42.94, -12.22) * mm, "end": v(47.28, -12.44) * mm});
            skArc(sketch, "E323", {"start": v(47.28, -12.44) * mm, "mid": v(53.75, -13.36) * mm, "end": v(60.17, -14.57) * mm});
            skArc(sketch, "E324", {"start": v(60.17, -14.57) * mm, "mid": v(66.15, -15.88) * mm, "end": v(72.09, -17.36) * mm});
            skArc(sketch, "E325", {"start": v(72.09, -17.36) * mm, "mid": v(72.45, -17.47) * mm, "end": v(72.8, -17.6) * mm});
            skArc(sketch, "E326", {"start": v(72.8, -17.6) * mm, "mid": v(72.91, -17.64) * mm, "end": v(72.96, -17.75) * mm});
            skArc(sketch, "E327", {"start": v(72.96, -17.75) * mm, "mid": v(72.43, -17.79) * mm, "end": v(71.9, -17.7) * mm});
            skArc(sketch, "E328", {"start": v(71.9, -17.7) * mm, "mid": v(61.4, -16.25) * mm, "end": v(50.82, -15.76) * mm});
            skArc(sketch, "E329", {"start": v(50.82, -15.76) * mm, "mid": v(43.57, -16.11) * mm, "end": v(36.36, -16.92) * mm});
            skArc(sketch, "E330", {"start": v(36.36, -16.92) * mm, "mid": v(32.11, -17.44) * mm, "end": v(27.85, -17.82) * mm});
            skArc(sketch, "E331", {"start": v(27.85, -17.82) * mm, "mid": v(22.97, -17.97) * mm, "end": v(18.1, -17.78) * mm});
            skArc(sketch, "E332", {"start": v(18.1, -17.78) * mm, "mid": v(12.65, -16.96) * mm, "end": v(7.35, -15.44) * mm});
            skArc(sketch, "E333", {"start": v(7.35, -15.44) * mm, "mid": v(2.34, -13.56) * mm, "end": v(-2.57, -11.47) * mm});
            skLineSegment(sketch, "E334", {"start": v(-2.57, -11.47) * mm, "end": v(-2.57, -11.47) * mm});
            skLineSegment(sketch, "E335", {"start": v(-2.57, -11.47) * mm, "end": v(-3.17, -11.2) * mm});
            skArc(sketch, "E336", {"start": v(-3.17, -11.2) * mm, "mid": v(-4.52, -10.7) * mm, "end": v(-5.87, -10.18) * mm});
            skArc(sketch, "E337", {"start": v(-5.87, -10.18) * mm, "mid": v(-9.83, -8.71) * mm, "end": v(-13.9, -7.58) * mm});
            skArc(sketch, "E338", {"start": v(-13.9, -7.58) * mm, "mid": v(-15.9, -7.27) * mm, "end": v(-17.94, -7.2) * mm});
            skArc(sketch, "E339", {"start": v(-17.94, -7.2) * mm, "mid": v(-19.92, -7.44) * mm, "end": v(-21.82, -8.02) * mm});
            skArc(sketch, "E340", {"start": v(-21.82, -8.02) * mm, "mid": v(-23.4, -8.9) * mm, "end": v(-24.8, -10.05) * mm});
            skArc(sketch, "E341", {"start": v(-24.8, -10.05) * mm, "mid": v(-25.63, -11.18) * mm, "end": v(-26.06, -12.5) * mm});
            skArc(sketch, "E342", {"start": v(-26.06, -12.5) * mm, "mid": v(-26.05, -13.39) * mm, "end": v(-25.8, -14.23) * mm});
            skArc(sketch, "E343", {"start": v(-25.8, -14.23) * mm, "mid": v(-25.09, -15.39) * mm, "end": v(-24.1, -16.32) * mm});
            skLineSegment(sketch, "E344", {"start": v(-24.1, -16.32) * mm, "end": v(-24.08, -16.34) * mm});
            skLineSegment(sketch, "E345", {"start": v(-24.08, -16.34) * mm, "end": v(-24.06, -16.35) * mm});
            skArc(sketch, "E346", {"start": v(-24.06, -16.35) * mm, "mid": v(-19.74, -18.33) * mm, "end": v(-15.09, -19.23) * mm});
            skArc(sketch, "E347", {"start": v(-15.09, -19.23) * mm, "mid": v(-10.2, -19.38) * mm, "end": v(-5.3, -19.15) * mm});
            skLineSegment(sketch, "E348", {"start": v(-5.3, -19.15) * mm, "end": v(-5.3, -19.15) * mm});
            skArc(sketch, "E349", {"start": v(-5.3, -19.15) * mm, "mid": v(-2.96, -19.02) * mm, "end": v(-0.62, -18.93) * mm});
            skArc(sketch, "E350", {"start": v(-0.62, -18.93) * mm, "mid": v(9.23, -19.63) * mm, "end": v(18.9, -21.64) * mm});
            skArc(sketch, "E351", {"start": v(18.9, -21.64) * mm, "mid": v(19.39, -21.78) * mm, "end": v(19.87, -21.94) * mm});
            skArc(sketch, "E352", {"start": v(19.87, -21.94) * mm, "mid": v(20.02, -21.99) * mm, "end": v(20.14, -22.1) * mm});
            skArc(sketch, "E353", {"start": v(20.14, -22.1) * mm, "mid": v(19.46, -22.06) * mm, "end": v(18.8, -21.92) * mm});
            skArc(sketch, "E354", {"start": v(18.8, -21.92) * mm, "mid": v(7.54, -20.93) * mm, "end": v(-3.7, -22.08) * mm});
            skArc(sketch, "E355", {"start": v(-3.7, -22.08) * mm, "mid": v(-3.73, -22.08) * mm, "end": v(-3.75, -22.08) * mm});
            skLineSegment(sketch, "E356", {"start": v(-3.75, -22.08) * mm, "end": v(-3.75, -22.08) * mm});
            skArc(sketch, "E357", {"start": v(-3.75, -22.08) * mm, "mid": v(-7.72, -22.77) * mm, "end": v(-11.72, -23.3) * mm});
            skArc(sketch, "E358", {"start": v(-11.72, -23.3) * mm, "mid": v(-14.71, -23.41) * mm, "end": v(-17.7, -23.07) * mm});
            skArc(sketch, "E359", {"start": v(-17.7, -23.07) * mm, "mid": v(-20.95, -22.1) * mm, "end": v(-24.05, -20.71) * mm});
            skArc(sketch, "E360", {"start": v(-24.05, -20.71) * mm, "mid": v(-28.65, -18.22) * mm, "end": v(-33.16, -15.56) * mm});
            skLineSegment(sketch, "E361", {"start": v(-33.16, -15.56) * mm, "end": v(-33.2, -15.53) * mm});
            skLineSegment(sketch, "E362", {"start": v(-33.2, -15.53) * mm, "end": v(-33.24, -15.52) * mm});
            skArc(sketch, "E363", {"start": v(-33.24, -15.52) * mm, "mid": v(-34.78, -14.83) * mm, "end": v(-36.3, -14.07) * mm});
            skLineSegment(sketch, "E364", {"start": v(-36.3, -14.07) * mm, "end": v(-36.3, -14.07) * mm});
            skArc(sketch, "E365", {"start": v(-36.3, -14.07) * mm, "mid": v(-38.1, -13.17) * mm, "end": v(-39.94, -12.33) * mm});
            skArc(sketch, "E366", {"start": v(-39.94, -12.33) * mm, "mid": v(-41.96, -11.56) * mm, "end": v(-44.05, -10.99) * mm});
            skArc(sketch, "E367", {"start": v(-44.05, -10.99) * mm, "mid": v(-48.7, -10.8) * mm, "end": v(-53.08, -12.37) * mm});
            skArc(sketch, "E368", {"start": v(-53.08, -12.37) * mm, "mid": v(-54.91, -13.92) * mm, "end": v(-56.3, -15.88) * mm});
            skArc(sketch, "E369", {"start": v(-56.3, -15.88) * mm, "mid": v(-57.16, -18.17) * mm, "end": v(-57.2, -20.6) * mm});
            skArc(sketch, "E370", {"start": v(-57.2, -20.6) * mm, "mid": v(-56.67, -22.12) * mm, "end": v(-55.7, -23.39) * mm});
            skArc(sketch, "E371", {"start": v(-55.7, -23.39) * mm, "mid": v(-53.56, -24.77) * mm, "end": v(-51.11, -25.48) * mm});
            skArc(sketch, "E372", {"start": v(-51.11, -25.48) * mm, "mid": v(-14.73, -30.82) * mm, "end": v(21.65, -36.13) * mm});
            skArc(sketch, "E373", {"start": v(21.65, -36.13) * mm, "mid": v(45.1, -39.55) * mm, "end": v(68.55, -42.94) * mm});
            skArc(sketch, "E374", {"start": v(68.55, -42.94) * mm, "mid": v(79.85, -44.58) * mm, "end": v(91.16, -46.13) * mm});
            skArc(sketch, "E375", {"start": v(91.16, -46.13) * mm, "mid": v(91.29, -46.14) * mm, "end": v(91.38, -46.23) * mm});
            skArc(sketch, "E376", {"start": v(91.38, -46.23) * mm, "mid": v(91.25, -46.3) * mm, "end": v(91.11, -46.28) * mm});
            skArc(sketch, "E377", {"start": v(91.11, -46.28) * mm, "mid": v(19.76, -40.29) * mm, "end": v(-51.6, -34.22) * mm});
            skLineSegment(sketch, "E378", {"start": v(-51.6, -34.22) * mm, "end": v(-51.62, -34.18) * mm});
            skLineSegment(sketch, "E379", {"start": v(-51.62, -34.18) * mm, "end": v(-51.91, -34.2) * mm});
            skArc(sketch, "E380", {"start": v(-51.91, -34.2) * mm, "mid": v(-57.36, -34.1) * mm, "end": v(-62.8, -33.79) * mm});
            skArc(sketch, "E381", {"start": v(-62.8, -33.79) * mm, "mid": v(-66.26, -33.48) * mm, "end": v(-69.7, -33.05) * mm});
            skArc(sketch, "E382", {"start": v(-69.7, -33.05) * mm, "mid": v(-72.24, -32.6) * mm, "end": v(-74.71, -31.84) * mm});
            skLineSegment(sketch, "E383", {"start": v(-74.71, -31.84) * mm, "end": v(-74.73, -31.84) * mm});
            skLineSegment(sketch, "E384", {"start": v(-74.73, -31.84) * mm, "end": v(-74.75, -31.83) * mm});
            skArc(sketch, "E385", {"start": v(-74.75, -31.83) * mm, "mid": v(-75.24, -31.67) * mm, "end": v(-75.72, -31.51) * mm});
            skArc(sketch, "E386", {"start": v(-75.72, -31.51) * mm, "mid": v(-77.95, -30.77) * mm, "end": v(-80.13, -29.9) * mm});
            skArc(sketch, "E387", {"start": v(-80.13, -29.9) * mm, "mid": v(-82.93, -28.47) * mm, "end": v(-85.53, -26.7) * mm});
            skArc(sketch, "E388", {"start": v(-85.53, -26.7) * mm, "mid": v(-88.32, -24.13) * mm, "end": v(-90.63, -21.1) * mm});
            skArc(sketch, "E389", {"start": v(-90.63, -21.1) * mm, "mid": v(-92.76, -16.83) * mm, "end": v(-94.09, -12.25) * mm});
            skArc(sketch, "E390", {"start": v(-94.09, -12.25) * mm, "mid": v(-94.19, -11.7) * mm, "end": v(-94.2, -11.16) * mm});
            skArc(sketch, "E391", {"start": v(-94.2, -11.16) * mm, "mid": v(-94.17, -10.97) * mm, "end": v(-94.02, -10.85) * mm});
            skArc(sketch, "E392", {"start": v(-94.02, -10.85) * mm, "mid": v(-93.62, -11.04) * mm, "end": v(-93.3, -11.34) * mm});
            skArc(sketch, "E393", {"start": v(-93.3, -11.34) * mm, "mid": v(-93.25, -11.38) * mm, "end": v(-93.2, -11.43) * mm});
            skLineSegment(sketch, "E394", {"start": v(-93.2, -11.43) * mm, "end": v(-93.18, -11.44) * mm});
            skLineSegment(sketch, "E395", {"start": v(-93.18, -11.44) * mm, "end": v(-93.16, -11.46) * mm});
            skArc(sketch, "E396", {"start": v(-93.16, -11.46) * mm, "mid": v(-86.93, -14.82) * mm, "end": v(-79.96, -16.05) * mm});
            skArc(sketch, "E397", {"start": v(-79.96, -16.05) * mm, "mid": v(-73.86, -15.42) * mm, "end": v(-68.08, -13.38) * mm});
            skArc(sketch, "E398", {"start": v(-68.08, -13.38) * mm, "mid": v(-63.5, -10.5) * mm, "end": v(-59.73, -6.63) * mm});
            skArc(sketch, "E399", {"start": v(-59.73, -6.63) * mm, "mid": v(-57.47, -2.62) * mm, "end": v(-56.6, 1.9) * mm});
            skArc(sketch, "E400", {"start": v(-56.6, 1.9) * mm, "mid": v(-56.91, 4.24) * mm, "end": v(-57.64, 6.47) * mm});
            skArc(sketch, "E401", {"start": v(-57.64, 6.47) * mm, "mid": v(-58.82, 8.75) * mm, "end": v(-60.31, 10.84) * mm});
            skArc(sketch, "E402", {"start": v(-60.31, 10.84) * mm, "mid": v(-64.54, 14.83) * mm, "end": v(-69.57, 17.74) * mm});
            skArc(sketch, "E403", {"start": v(-69.57, 17.74) * mm, "mid": v(-75.65, 19.6) * mm, "end": v(-82, 19.8) * mm});
            skArc(sketch, "E404", {"start": v(-82, 19.8) * mm, "mid": v(-87.86, 18.25) * mm, "end": v(-93.02, 15.06) * mm});
            skArc(sketch, "E405", {"start": v(-93.02, 15.06) * mm, "mid": v(-93.13, 15) * mm, "end": v(-93.24, 14.93) * mm});
            skArc(sketch, "E406", {"start": v(-93.24, 14.93) * mm, "mid": v(-93.5, 14.8) * mm, "end": v(-93.78, 14.83) * mm});
            skArc(sketch, "E407", {"start": v(-93.78, 14.83) * mm, "mid": v(-93.83, 14.96) * mm, "end": v(-93.83, 15.1) * mm});
            skArc(sketch, "E408", {"start": v(-93.83, 15.1) * mm, "mid": v(-93.75, 15.4) * mm, "end": v(-93.64, 15.67) * mm});
            skArc(sketch, "E409", {"start": v(-93.64, 15.67) * mm, "mid": v(-92.04, 18.97) * mm, "end": v(-90.27, 22.18) * mm});
            skArc(sketch, "E410", {"start": v(-90.27, 22.18) * mm, "mid": v(-88, 25.67) * mm, "end": v(-85.38, 28.9) * mm});
            skArc(sketch, "E411", {"start": v(-85.38, 28.9) * mm, "mid": v(-82.26, 31.87) * mm, "end": v(-78.69, 34.26) * mm});
            skArc(sketch, "E412", {"start": v(-78.69, 34.26) * mm, "mid": v(-74.45, 35.96) * mm, "end": v(-69.93, 36.64) * mm});
            skLineSegment(sketch, "E413", {"start": v(-69.93, 36.64) * mm, "end": v(-69.9, 36.64) * mm});
            skLineSegment(sketch, "E414", {"start": v(-69.9, 36.64) * mm, "end": v(-69.85, 36.65) * mm});
            skArc(sketch, "E415", {"start": v(-69.85, 36.65) * mm, "mid": v(-66.52, 36.98) * mm, "end": v(-63.18, 37.21) * mm});
            skArc(sketch, "E416", {"start": v(-63.18, 37.21) * mm, "mid": v(-55.67, 37.72) * mm, "end": v(-48.16, 38.2) * mm});
            skArc(sketch, "E417", {"start": v(-48.16, 38.2) * mm, "mid": v(-25.3, 39.58) * mm, "end": v(-2.43, 40.92) * mm});
            skArc(sketch, "E418", {"start": v(-2.43, 40.92) * mm, "mid": v(41.92, 43.47) * mm, "end": v(86.28, 45.96) * mm});
            skArc(sketch, "E419", {"start": v(86.28, 45.96) * mm, "mid": v(87.07, 45.99) * mm, "end": v(87.85, 45.9) * mm});
            skArc(sketch, "E420", {"start": v(87.85, 45.9) * mm, "mid": v(87.88, 45.88) * mm, "end": v(87.86, 45.84) * mm});
            skArc(sketch, "E421", {"start": v(87.86, 45.84) * mm, "mid": v(87.74, 45.8) * mm, "end": v(87.63, 45.76) * mm});
            skArc(sketch, "E422", {"start": v(87.63, 45.76) * mm, "mid": v(86.96, 45.65) * mm, "end": v(86.28, 45.57) * mm});
            skArc(sketch, "E423", {"start": v(86.28, 45.57) * mm, "mid": v(45.87, 40.95) * mm, "end": v(5.47, 36.27) * mm});
            skLineSegment(sketch, "E424", {"start": v(5.47, 36.27) * mm, "end": v(5.34, 36.25) * mm});
            skLineSegment(sketch, "E425", {"start": v(5.34, 36.25) * mm, "end": v(5.33, 36.25) * mm});
            skArc(sketch, "E426", {"start": v(5.33, 36.25) * mm, "mid": v(-22.34, 33.04) * mm, "end": v(-50.02, 29.89) * mm});
            skArc(sketch, "E427", {"start": v(-50.02, 29.89) * mm, "mid": v(-52.4, 29.32) * mm, "end": v(-54.6, 28.26) * mm});
            skArc(sketch, "E428", {"start": v(-54.6, 28.26) * mm, "mid": v(-56.1, 26.95) * mm, "end": v(-57.07, 25.24) * mm});
            skSolve(sketch);
        }
        {
            var Q0;
            Q0 = qSketchRegion(id + "F0", true);
            extrude(context, id + "F1", {"entities" : qUnion([Q0]), "depth" : 3 * mm, "offsetDistance" : 25 * mm});
        }
    });
